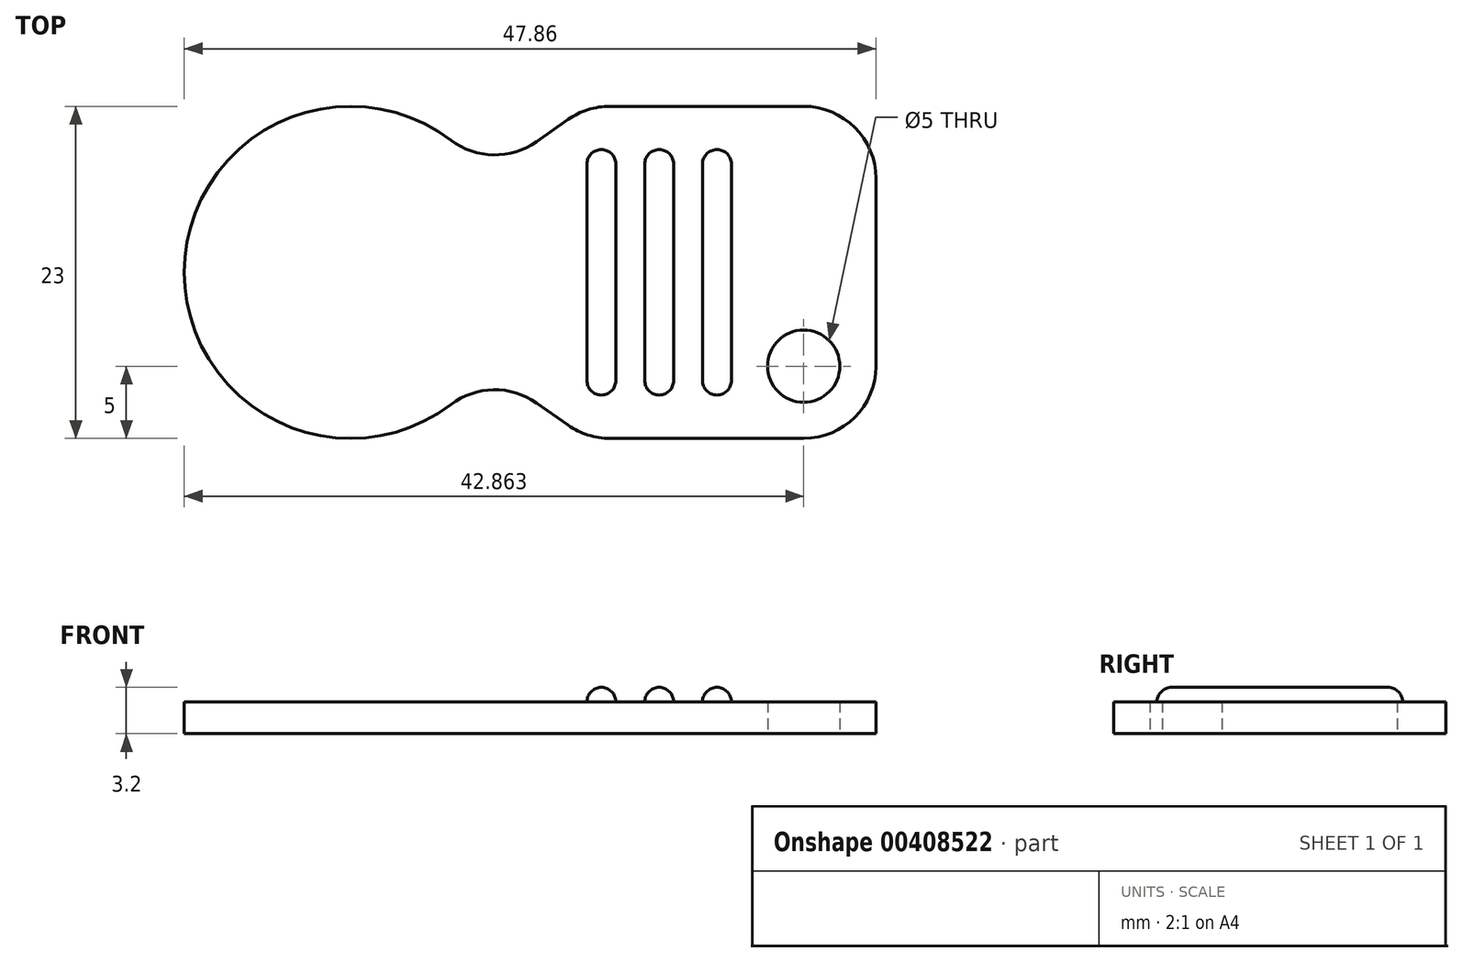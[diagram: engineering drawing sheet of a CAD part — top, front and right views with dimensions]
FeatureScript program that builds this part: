
annotation { "Feature Type Name" : "Feature", "Feature Type Description" : "" }
export const myFeature = defineFeature(function(context is Context, id is Id, definition is map)
    precondition{}
    {
        {
            var Q0;
            Q0=qCreatedBy(makeId("Top.planeOp"),FACE);
            var sketch = newSketch(context, id + "F0", { "sketchPlane" : qUnion([Q0])});
            skCircle(sketch, "E0", {"center": v(0, 0) * mm, "radius": 11.5 * mm});
            skSolve(sketch);
        }
        {
            var Q0;
            Q0=makeQuery(id+"F0.imprint","IMPRINT",FACE,{"disambiguationData":[TD([[makeQuery(id+"F0.imprint","IMPRINT",EDGE,{"derivedFrom":sQuery(id+"F0.wireOp",EDGE,"E0")}),1.0]])]});
            extrude(context, id + "F1", {"entities" : qUnion([Q0]), "depth" : 2.2 * mm});
        }
        {
            var Q0;
            Q0=qCreatedBy(makeId("Top.planeOp"),FACE);
            var sketch = newSketch(context, id + "F2", { "sketchPlane" : qUnion([Q0])});
            skLineSegment(sketch, "E1", {"start": v(0, 0) * mm, "end": v(16.36, -11.5) * mm});
            skLineSegment(sketch, "E2", {"start": v(16.36, -11.5) * mm, "end": v(36.36, -11.5) * mm});
            skLineSegment(sketch, "E3", {"start": v(36.36, -11.5) * mm, "end": v(36.36, 11.5) * mm});
            skLineSegment(sketch, "E4", {"start": v(36.36, 11.5) * mm, "end": v(16.36, 11.5) * mm});
            skLineSegment(sketch, "E5", {"start": v(16.36, 11.5) * mm, "end": v(0, 0) * mm});
            skSolve(sketch);
        }
        {
            var Q0;
            Q0=makeQuery(id+"F2.imprint","IMPRINT",FACE,{"disambiguationData":[TD([[makeQuery(id+"F2.imprint","IMPRINT",EDGE,{"derivedFrom":sQuery(id+"F2.wireOp",EDGE,"E1")}),1.0]])]});
            extrude(context, id + "F3", {"entities" : qUnion([Q0]), "operationType" : NewBodyOperationType.ADD, "depth" : 2.2 * mm});
        }
        {
            var Q0;
            Q0=makeQuery(id+"F3.boolean.opBoolean","MERGE",FACE,{"derivedFrom":[makeQuery(id+"F1.opExtrude","CAP_FACE",FACE,{"disambiguationData":[OSD([sQuery(id+"F0.wireOp",EDGE,"E0")])],"isStart":true}),makeQuery(id+"F3.opExtrude","CAP_FACE",FACE,{"disambiguationData":[OSD([sQuery(id+"F2.wireOp",EDGE,"E1"),sQuery(id+"F2.wireOp",EDGE,"E2"),sQuery(id+"F2.wireOp",EDGE,"E3"),sQuery(id+"F2.wireOp",EDGE,"E4"),sQuery(id+"F2.wireOp",EDGE,"E5")])],"isStart":true})]});
            var sketch = newSketch(context, id + "F4", { "sketchPlane" : qUnion([Q0])});
            skCircle(sketch, "E6", {"center": v(31.36, 6.5) * mm, "radius": 2.5 * mm});
            skSolve(sketch);
        }
        {
            var Q0;
            Q0=makeQuery(id+"F4.imprint","IMPRINT",FACE,{"disambiguationData":[TD([[makeQuery(id+"F4.imprint","IMPRINT",EDGE,{"derivedFrom":sQuery(id+"F4.wireOp",EDGE,"E6")}),1.0]])]});
            extrude(context, id + "F5", {"entities" : qUnion([Q0]), "operationType" : NewBodyOperationType.REMOVE, "endBound" : BoundingType.THROUGH_ALL, "oppositeDirection" : true, "depth" : 25 * mm});
        }
        {
            var Q0;
            Q0=makeQuery(id+"F3.opExtrude","SWEPT_EDGE",EDGE,{"disambiguationData":[OSD([sQuery(id+"F2.wireOp",EDGE,"E2"),sQuery(id+"F2.wireOp",EDGE,"E3")])]});
            var Q1;
            Q1=makeQuery(id+"F3.opExtrude","SWEPT_EDGE",EDGE,{"disambiguationData":[OSD([sQuery(id+"F2.wireOp",EDGE,"E3"),sQuery(id+"F2.wireOp",EDGE,"E4")])]});
            var Q2;
            Q2=makeQuery(id+"F3.opExtrude","SWEPT_EDGE",EDGE,{"disambiguationData":[OSD([sQuery(id+"F2.wireOp",EDGE,"E1"),sQuery(id+"F2.wireOp",EDGE,"E2")])]});
            var Q3;
            Q3=makeQuery(id+"F3.boolean.opBoolean","INTERSECT",EDGE,{"derivedFrom":[makeQuery(id+"F1.opExtrude","SWEPT_FACE",FACE,{"disambiguationData":[OSD([sQuery(id+"F0.wireOp",EDGE,"E0")])]}),makeQuery(id+"F3.opExtrude","SWEPT_FACE",FACE,{"disambiguationData":[OSD([sQuery(id+"F2.wireOp",EDGE,"E1")])]})]});
            var Q4;
            Q4=makeQuery(id+"F3.boolean.opBoolean","INTERSECT",EDGE,{"derivedFrom":[makeQuery(id+"F1.opExtrude","SWEPT_FACE",FACE,{"disambiguationData":[OSD([sQuery(id+"F0.wireOp",EDGE,"E0")])]}),makeQuery(id+"F3.opExtrude","SWEPT_FACE",FACE,{"disambiguationData":[OSD([sQuery(id+"F2.wireOp",EDGE,"E5")])]})]});
            var Q5;
            Q5=makeQuery(id+"F3.opExtrude","SWEPT_EDGE",EDGE,{"disambiguationData":[OSD([sQuery(id+"F2.wireOp",EDGE,"E4"),sQuery(id+"F2.wireOp",EDGE,"E5")])]});
            fillet(context, id + "F6", {"entities" : qUnion([Q0, Q1, Q2, Q3, Q4, Q5]), "radius" : 5 * mm, "tangentPropagation" : true, "allowEdgeOverflow" : false});
        }
        {
            var Q0;
            Q0=makeQuery(id+"F3.boolean.opBoolean","MERGE",FACE,{"derivedFrom":[makeQuery(id+"F1.opExtrude","CAP_FACE",FACE,{"disambiguationData":[OSD([sQuery(id+"F0.wireOp",EDGE,"E0")])],"isStart":false}),makeQuery(id+"F3.opExtrude","CAP_FACE",FACE,{"disambiguationData":[OSD([sQuery(id+"F2.wireOp",EDGE,"E1"),sQuery(id+"F2.wireOp",EDGE,"E2"),sQuery(id+"F2.wireOp",EDGE,"E3"),sQuery(id+"F2.wireOp",EDGE,"E4"),sQuery(id+"F2.wireOp",EDGE,"E5")])],"isStart":false})]});
            var sketch = newSketch(context, id + "F7", { "sketchPlane" : qUnion([Q0])});
            skLineSegment(sketch, "E7.bottom", {"start": v(16.36, 8.5) * mm, "end": v(18.36, 8.5) * mm});
            skLineSegment(sketch, "E7.top", {"start": v(16.36, -8.5) * mm, "end": v(18.36, -8.5) * mm});
            skLineSegment(sketch, "E7.left", {"start": v(16.36, 8.5) * mm, "end": v(16.36, -8.5) * mm});
            skLineSegment(sketch, "E7.right", {"start": v(18.36, 8.5) * mm, "end": v(18.36, -8.5) * mm});
            skLineSegment(sketch, "E8.bottom", {"start": v(20.36, 8.5) * mm, "end": v(22.36, 8.5) * mm});
            skLineSegment(sketch, "E8.top", {"start": v(20.36, -8.5) * mm, "end": v(22.36, -8.5) * mm});
            skLineSegment(sketch, "E8.left", {"start": v(20.36, 8.5) * mm, "end": v(20.36, -8.5) * mm});
            skLineSegment(sketch, "E8.right", {"start": v(22.36, 8.5) * mm, "end": v(22.36, -8.5) * mm});
            skLineSegment(sketch, "E9.bottom", {"start": v(24.36, 8.5) * mm, "end": v(26.36, 8.5) * mm});
            skLineSegment(sketch, "E9.top", {"start": v(24.36, -8.5) * mm, "end": v(26.36, -8.5) * mm});
            skLineSegment(sketch, "E9.left", {"start": v(24.36, 8.5) * mm, "end": v(24.36, -8.5) * mm});
            skLineSegment(sketch, "E9.right", {"start": v(26.36, 8.5) * mm, "end": v(26.36, -8.5) * mm});
            skSolve(sketch);
        }
        {
            var Q0;
            Q0=makeQuery(id+"F7.imprint","IMPRINT",FACE,{"disambiguationData":[TD([[makeQuery(id+"F7.imprint","IMPRINT",EDGE,{"derivedFrom":sQuery(id+"F7.wireOp",EDGE,"E7.bottom")}),-1.0]])]});
            var Q1;
            Q1=makeQuery(id+"F7.imprint","IMPRINT",FACE,{"disambiguationData":[TD([[makeQuery(id+"F7.imprint","IMPRINT",EDGE,{"derivedFrom":sQuery(id+"F7.wireOp",EDGE,"E8.bottom")}),-1.0]])]});
            var Q2;
            Q2=makeQuery(id+"F7.imprint","IMPRINT",FACE,{"disambiguationData":[TD([[makeQuery(id+"F7.imprint","IMPRINT",EDGE,{"derivedFrom":sQuery(id+"F7.wireOp",EDGE,"E9.bottom")}),-1.0]])]});
            extrude(context, id + "F8", {"entities" : qUnion([Q0, Q1, Q2]), "operationType" : NewBodyOperationType.ADD, "depth" : 1 * mm});
        }
        {
            var Q0;
            Q0=makeQuery(id+"F8.opExtrude","SWEPT_EDGE",EDGE,{"disambiguationData":[OSD([sQuery(id+"F7.wireOp",EDGE,"E7.top"),sQuery(id+"F7.wireOp",EDGE,"E7.left")])]});
            var Q1;
            Q1=makeQuery(id+"F8.opExtrude","SWEPT_EDGE",EDGE,{"disambiguationData":[OSD([sQuery(id+"F7.wireOp",EDGE,"E7.top"),sQuery(id+"F7.wireOp",EDGE,"E7.right")])]});
            var Q2;
            Q2=makeQuery(id+"F8.opExtrude","SWEPT_EDGE",EDGE,{"disambiguationData":[OSD([sQuery(id+"F7.wireOp",EDGE,"E8.top"),sQuery(id+"F7.wireOp",EDGE,"E8.left")])]});
            var Q3;
            Q3=makeQuery(id+"F8.opExtrude","SWEPT_EDGE",EDGE,{"disambiguationData":[OSD([sQuery(id+"F7.wireOp",EDGE,"E8.top"),sQuery(id+"F7.wireOp",EDGE,"E8.right")])]});
            var Q4;
            Q4=makeQuery(id+"F8.opExtrude","SWEPT_EDGE",EDGE,{"disambiguationData":[OSD([sQuery(id+"F7.wireOp",EDGE,"E9.top"),sQuery(id+"F7.wireOp",EDGE,"E9.left")])]});
            var Q5;
            Q5=makeQuery(id+"F8.opExtrude","SWEPT_EDGE",EDGE,{"disambiguationData":[OSD([sQuery(id+"F7.wireOp",EDGE,"E9.top"),sQuery(id+"F7.wireOp",EDGE,"E9.right")])]});
            var Q6;
            Q6=makeQuery(id+"F8.opExtrude","SWEPT_EDGE",EDGE,{"disambiguationData":[OSD([sQuery(id+"F7.wireOp",EDGE,"E9.bottom"),sQuery(id+"F7.wireOp",EDGE,"E9.right")])]});
            var Q7;
            Q7=makeQuery(id+"F8.opExtrude","SWEPT_EDGE",EDGE,{"disambiguationData":[OSD([sQuery(id+"F7.wireOp",EDGE,"E7.bottom"),sQuery(id+"F7.wireOp",EDGE,"E7.left")])]});
            var Q8;
            Q8=makeQuery(id+"F8.opExtrude","SWEPT_EDGE",EDGE,{"disambiguationData":[OSD([sQuery(id+"F7.wireOp",EDGE,"E9.bottom"),sQuery(id+"F7.wireOp",EDGE,"E9.left")])]});
            var Q9;
            Q9=makeQuery(id+"F8.opExtrude","SWEPT_EDGE",EDGE,{"disambiguationData":[OSD([sQuery(id+"F7.wireOp",EDGE,"E8.bottom"),sQuery(id+"F7.wireOp",EDGE,"E8.right")])]});
            var Q10;
            Q10=makeQuery(id+"F8.opExtrude","SWEPT_EDGE",EDGE,{"disambiguationData":[OSD([sQuery(id+"F7.wireOp",EDGE,"E7.bottom"),sQuery(id+"F7.wireOp",EDGE,"E7.right")])]});
            var Q11;
            Q11=makeQuery(id+"F8.opExtrude","SWEPT_EDGE",EDGE,{"disambiguationData":[OSD([sQuery(id+"F7.wireOp",EDGE,"E8.bottom"),sQuery(id+"F7.wireOp",EDGE,"E8.left")])]});
            var Q12;
            Q12=makeQuery(id+"F8.opExtrude","CAP_EDGE",EDGE,{"disambiguationData":[OSD([sQuery(id+"F7.wireOp",EDGE,"E8.left")])],"isStart":false});
            var Q13;
            Q13=makeQuery(id+"F8.opExtrude","CAP_EDGE",EDGE,{"disambiguationData":[OSD([sQuery(id+"F7.wireOp",EDGE,"E8.right")])],"isStart":false});
            var Q14;
            Q14=makeQuery(id+"F8.opExtrude","CAP_EDGE",EDGE,{"disambiguationData":[OSD([sQuery(id+"F7.wireOp",EDGE,"E8.bottom")])],"isStart":false});
            var Q15;
            Q15=makeQuery(id+"F8.opExtrude","CAP_EDGE",EDGE,{"disambiguationData":[OSD([sQuery(id+"F7.wireOp",EDGE,"E8.top")])],"isStart":false});
            var Q16;
            Q16=makeQuery(id+"F8.opExtrude","CAP_EDGE",EDGE,{"disambiguationData":[OSD([sQuery(id+"F7.wireOp",EDGE,"E7.right")])],"isStart":false});
            var Q17;
            Q17=makeQuery(id+"F8.opExtrude","CAP_EDGE",EDGE,{"disambiguationData":[OSD([sQuery(id+"F7.wireOp",EDGE,"E7.left")])],"isStart":false});
            var Q18;
            Q18=makeQuery(id+"F8.opExtrude","CAP_EDGE",EDGE,{"disambiguationData":[OSD([sQuery(id+"F7.wireOp",EDGE,"E7.bottom")])],"isStart":false});
            var Q19;
            Q19=makeQuery(id+"F8.opExtrude","CAP_EDGE",EDGE,{"disambiguationData":[OSD([sQuery(id+"F7.wireOp",EDGE,"E7.top")])],"isStart":false});
            var Q20;
            Q20=makeQuery(id+"F8.opExtrude","CAP_EDGE",EDGE,{"disambiguationData":[OSD([sQuery(id+"F7.wireOp",EDGE,"E9.right")])],"isStart":false});
            var Q21;
            Q21=makeQuery(id+"F8.opExtrude","CAP_EDGE",EDGE,{"disambiguationData":[OSD([sQuery(id+"F7.wireOp",EDGE,"E9.left")])],"isStart":false});
            var Q22;
            Q22=makeQuery(id+"F8.opExtrude","CAP_EDGE",EDGE,{"disambiguationData":[OSD([sQuery(id+"F7.wireOp",EDGE,"E9.bottom")])],"isStart":false});
            var Q23;
            Q23=makeQuery(id+"F8.opExtrude","CAP_EDGE",EDGE,{"disambiguationData":[OSD([sQuery(id+"F7.wireOp",EDGE,"E9.top")])],"isStart":false});
            fillet(context, id + "F9", {"entities" : qUnion([Q0, Q1, Q2, Q3, Q4, Q5, Q6, Q7, Q8, Q9, Q10, Q11, Q12, Q13, Q14, Q15, Q16, Q17, Q18, Q19, Q20, Q21, Q22, Q23]), "radius" : 1 * mm, "tangentPropagation" : true, "allowEdgeOverflow" : false});
        }
    });
